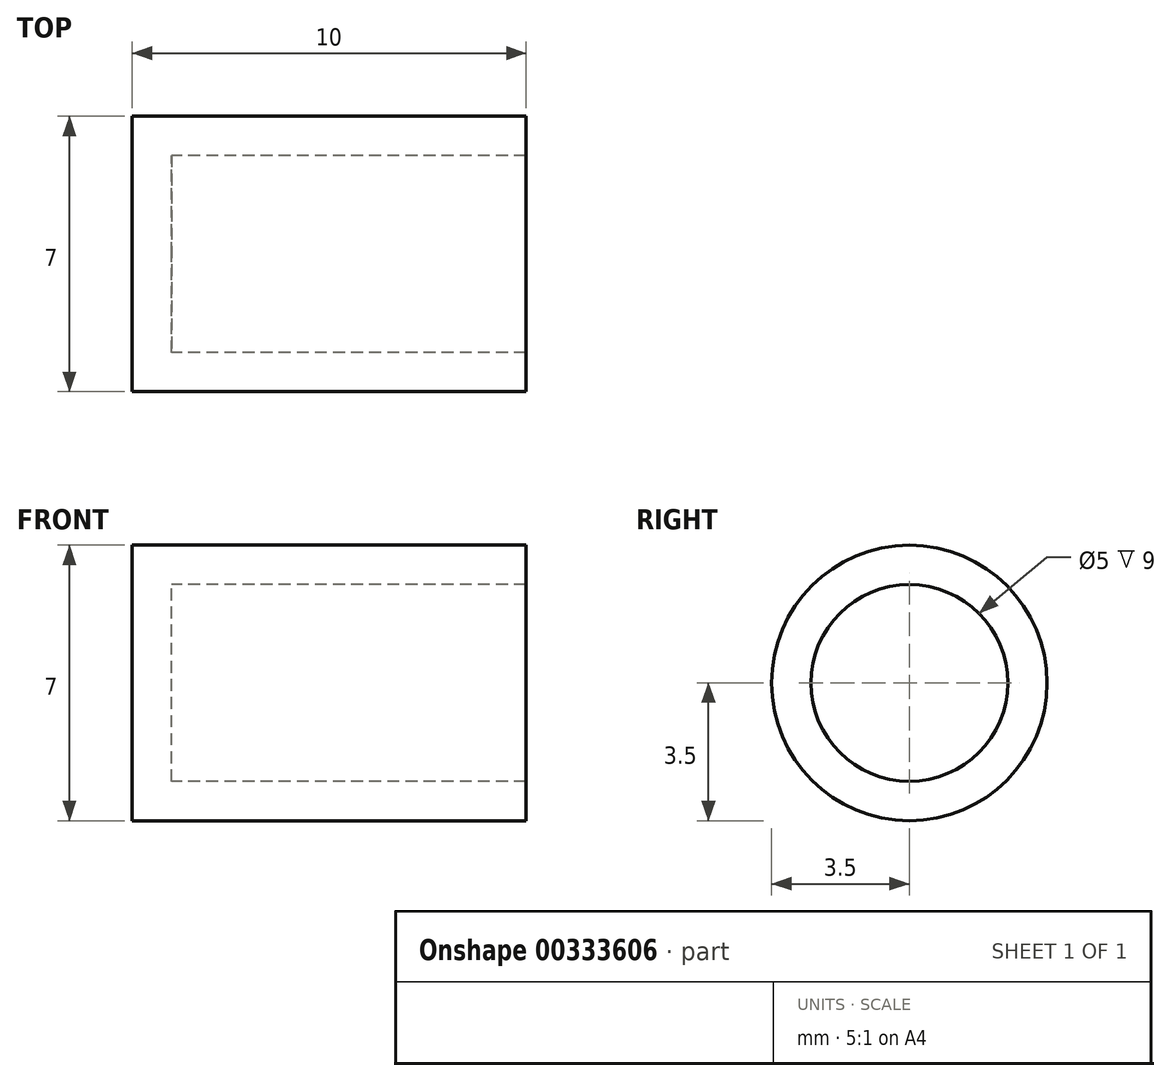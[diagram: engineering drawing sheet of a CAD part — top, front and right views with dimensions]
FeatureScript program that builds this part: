
annotation { "Feature Type Name" : "Feature", "Feature Type Description" : "" }
export const myFeature = defineFeature(function(context is Context, id is Id, definition is map)
    precondition{}
    {
        {
            var Q0;
            Q0=qCreatedBy(makeId("Right.planeOp"),FACE);
            var sketch = newSketch(context, id + "F0", { "sketchPlane" : qUnion([Q0])});
            skCircle(sketch, "E0", {"center": v(0, 0) * mm, "radius": 3.5 * mm});
            skCircle(sketch, "E1", {"center": v(0, 0) * mm, "radius": 2.2 * mm});
            skSolve(sketch);
        }
        {
            var Q0;
            Q0=makeQuery(id+"F0.imprint","IMPRINT",FACE,{"disambiguationData":[TD([[makeQuery(id+"F0.imprint","IMPRINT",EDGE,{"derivedFrom":sQuery(id+"F0.wireOp",EDGE,"E0")}),1.0]])]});
            var Q1;
            Q1=makeQuery(id+"F0.imprint","IMPRINT",FACE,{"disambiguationData":[TD([[makeQuery(id+"F0.imprint","IMPRINT",EDGE,{"derivedFrom":sQuery(id+"F0.wireOp",EDGE,"E1")}),1.0]])]});
            extrude(context, id + "F1", {"entities" : qUnion([Q0, Q1]), "depth" : 10 * mm});
        }
        {
            var Q0;
            Q0=makeQuery(id+"F1.opExtrude","CAP_FACE",FACE,{"disambiguationData":[OSD([sQuery(id+"F0.wireOp",EDGE,"E0")])],"isStart":false});
            shell(context, id + "F2", {"entities" : qUnion([Q0]), "thickness" : 1 * mm});
        }
    });
